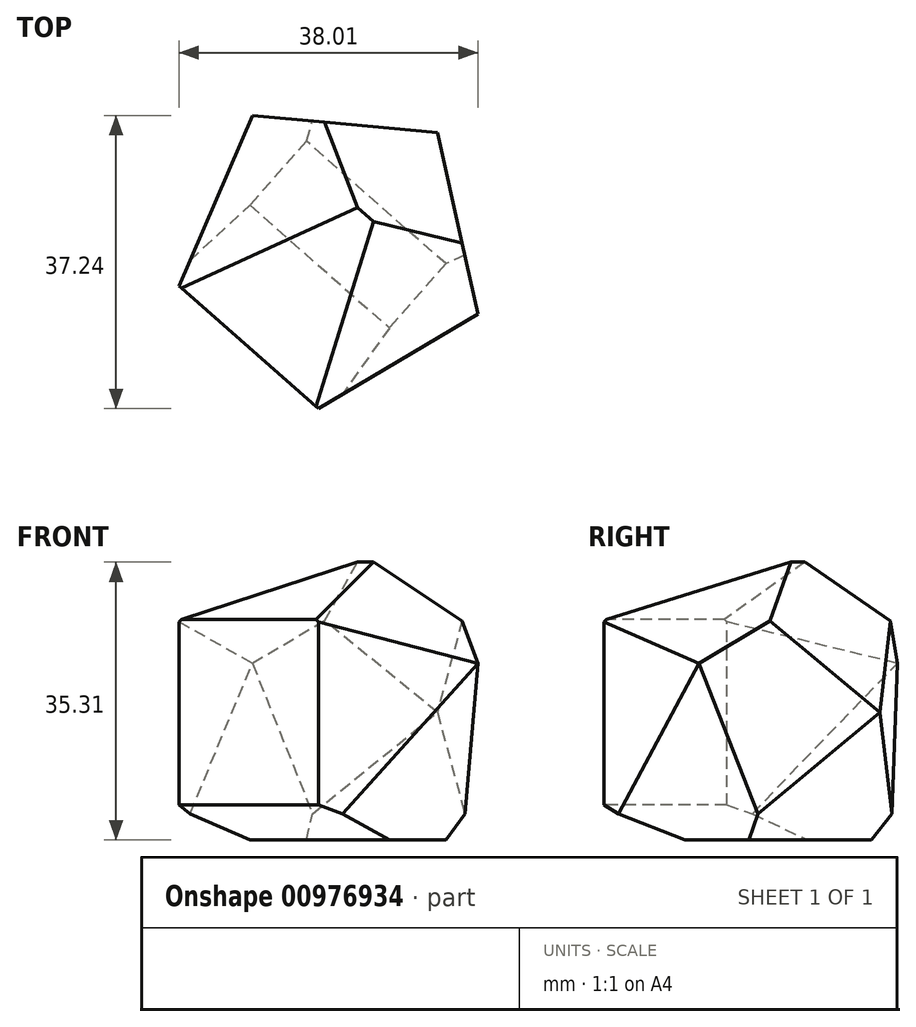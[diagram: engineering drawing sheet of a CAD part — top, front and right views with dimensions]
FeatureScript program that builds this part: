
annotation { "Feature Type Name" : "Feature", "Feature Type Description" : "" }
export const myFeature = defineFeature(function(context is Context, id is Id, definition is map)
    precondition{}
    {
        {
            var Q0;
            Q0=qCreatedBy(makeId("Top.planeOp"),FACE);
            var sketch = newSketch(context, id + "F0", { "sketchPlane" : qUnion([Q0])});
            skCircle(sketch, "E0.cCircle", {"center": v(-21.7, 9.51) * mm, "radius": 16.23 * mm, "construction": true});
            skLineSegment(sketch, "E0.0", {"start": v(-3.28, 1.57) * mm, "end": v(-23.57, -10.47) * mm});
            skLineSegment(sketch, "E0.1", {"start": v(-23.57, -10.47) * mm, "end": v(-41.29, 5.1) * mm});
            skLineSegment(sketch, "E0.2", {"start": v(-41.29, 5.1) * mm, "end": v(-31.95, 26.77) * mm});
            skLineSegment(sketch, "E0.3", {"start": v(-31.95, 26.77) * mm, "end": v(-8.46, 24.58) * mm});
            skLineSegment(sketch, "E0.4", {"start": v(-8.46, 24.58) * mm, "end": v(-3.28, 1.57) * mm});
            skPoint(sketch, "E0.0.midPoint", {"position": v(-13.42, -4.45) * mm});
            skLineSegment(sketch, "E1", {"start": v(-8.46, 24.58) * mm, "end": v(-33.17, -3.52) * mm});
            skLineSegment(sketch, "E2", {"start": v(-21.7, 9.51) * mm, "end": v(-34.53, 20.78) * mm});
            skLineSegment(sketch, "E3", {"start": v(-34.53, 20.78) * mm, "end": v(-8.89, -1.76) * mm});
            skSolve(sketch);
        }
        {
            var Q0;
            {var subQ0=sQuery(id+"F0.wireOp",EDGE,"E3");var subQ3=sQuery(id+"F0.wireOp",EDGE,"E0.4");var subQ4=makeQuery(id+"F0.imprint","IMPRINT",EDGE,{"derivedFrom":subQ0});Q0=qUnion([makeQuery(id+"F0.imprint","IMPRINT",FACE,{"disambiguationData":[TD([[subQ4,-1.0]])]}),makeQuery(id+"F0.imprint","IMPRINT",FACE,{"disambiguationData":[TD([[makeQuery(id+"F0.imprint","IMPRINT",EDGE,{"derivedFrom":subQ3}),-1.0]])]})]);}
            var Q1;
            {var subQ0=sQuery(id+"F0.wireOp",EDGE,"E0.3");var subQ2=sQuery(id+"F0.wireOp",EDGE,"E2");var subQ4=makeQuery(id+"F0.imprint","IMPRINT",EDGE,{"derivedFrom":subQ2});Q1=qUnion([makeQuery(id+"F0.imprint","IMPRINT",FACE,{"disambiguationData":[TD([[subQ4,1.0]])]}),makeQuery(id+"F0.imprint","IMPRINT",FACE,{"disambiguationData":[TD([[makeQuery(id+"F0.imprint","IMPRINT",EDGE,{"derivedFrom":subQ0}),-1.0]])]})]);}
            var Q2;
            {var subQ0=sQuery(id+"F0.wireOp",EDGE,"E0.3");Q2=makeQuery(id+"F0.imprint","IMPRINT",FACE,{"disambiguationData":[TD([[makeQuery(id+"F0.imprint","IMPRINT",EDGE,{"derivedFrom":subQ0}),-1.0]])]});}
            extrude(context, id + "F1", {"entities" : qUnion([Q0, Q1, Q2]), "oppositeDirection" : true, "depth" : 25.4 * mm, "offsetDistance" : 25.4 * mm});
        }
        {
            var Q0;
            Q0=makeQuery(id+"F1.opExtrude","CAP_FACE",FACE,{"disambiguationData":[OSD([sQuery(id+"F0.wireOp",EDGE,"E0.0"),sQuery(id+"F0.wireOp",EDGE,"E0.1"),sQuery(id+"F0.wireOp",EDGE,"E0.2"),sQuery(id+"F0.wireOp",EDGE,"E0.3"),sQuery(id+"F0.wireOp",EDGE,"E0.4")])],"isStart":true});
            extrude(context, id + "F2", {"entities" : qUnion([Q0]), "operationType" : NewBodyOperationType.ADD, "depth" : 25.4 * mm, "offsetDistance" : 25.4 * mm});
        }
        {
            var Q0;
            Q0=makeQuery(id+"F1.opExtrude","SWEPT_BODY",BODY,{"disambiguationData":[OSD([sQuery(id+"F0.wireOp",EDGE,"E0.0"),sQuery(id+"F0.wireOp",EDGE,"E0.1"),sQuery(id+"F0.wireOp",EDGE,"E0.2"),sQuery(id+"F0.wireOp",EDGE,"E0.3"),sQuery(id+"F0.wireOp",EDGE,"E0.4")])]});
            var Q1;
            Q1=sQuery(id+"F0.wireOp",EDGE,"E1");
            circularPattern(context, id + "F3", {"entities" : qUnion([Q0]), "axis" : qUnion([Q1]), "angle" : 90 * degree, "instanceCount" : 2, "oppositeDirection" : true, "equalSpace" : true});
        }
        {
            var Q0;
            Q0=makeQuery(id+"F1.opExtrude","SWEPT_BODY",BODY,{"disambiguationData":[OSD([sQuery(id+"F0.wireOp",EDGE,"E0.0"),sQuery(id+"F0.wireOp",EDGE,"E0.1"),sQuery(id+"F0.wireOp",EDGE,"E0.2"),sQuery(id+"F0.wireOp",EDGE,"E0.3"),sQuery(id+"F0.wireOp",EDGE,"E0.4")])]});
            var Q1;
            Q1=sQuery(id+"F0.wireOp",EDGE,"E3");
            circularPattern(context, id + "F4", {"entities" : qUnion([Q0]), "axis" : qUnion([Q1]), "angle" : 90 * degree, "instanceCount" : 2, "equalSpace" : true});
        }
        {
            var Q0;
            Q0=makeQuery(id+"F3.opPattern","COPY",BODY,{"derivedFrom":makeQuery(id+"F1.opExtrude","SWEPT_BODY",BODY,{"disambiguationData":[OSD([sQuery(id+"F0.wireOp",EDGE,"E0.0"),sQuery(id+"F0.wireOp",EDGE,"E0.1"),sQuery(id+"F0.wireOp",EDGE,"E0.2"),sQuery(id+"F0.wireOp",EDGE,"E0.3"),sQuery(id+"F0.wireOp",EDGE,"E0.4")])]}),"instanceName":"1"});
            var Q1;
            Q1=makeQuery(id+"F4.opPattern","COPY",BODY,{"derivedFrom":makeQuery(id+"F1.opExtrude","SWEPT_BODY",BODY,{"disambiguationData":[OSD([sQuery(id+"F0.wireOp",EDGE,"E0.0"),sQuery(id+"F0.wireOp",EDGE,"E0.1"),sQuery(id+"F0.wireOp",EDGE,"E0.2"),sQuery(id+"F0.wireOp",EDGE,"E0.3"),sQuery(id+"F0.wireOp",EDGE,"E0.4")])]}),"instanceName":"1"});
            var Q2;
            Q2=makeQuery(id+"F1.opExtrude","SWEPT_BODY",BODY,{"disambiguationData":[OSD([sQuery(id+"F0.wireOp",EDGE,"E0.0"),sQuery(id+"F0.wireOp",EDGE,"E0.1"),sQuery(id+"F0.wireOp",EDGE,"E0.2"),sQuery(id+"F0.wireOp",EDGE,"E0.3"),sQuery(id+"F0.wireOp",EDGE,"E0.4")])]});
            booleanBodies(context, id + "F5", {"operationType" : BooleanOperationType.INTERSECTION, "tools" : qUnion([Q0, Q1, Q2])});
        }
    });
